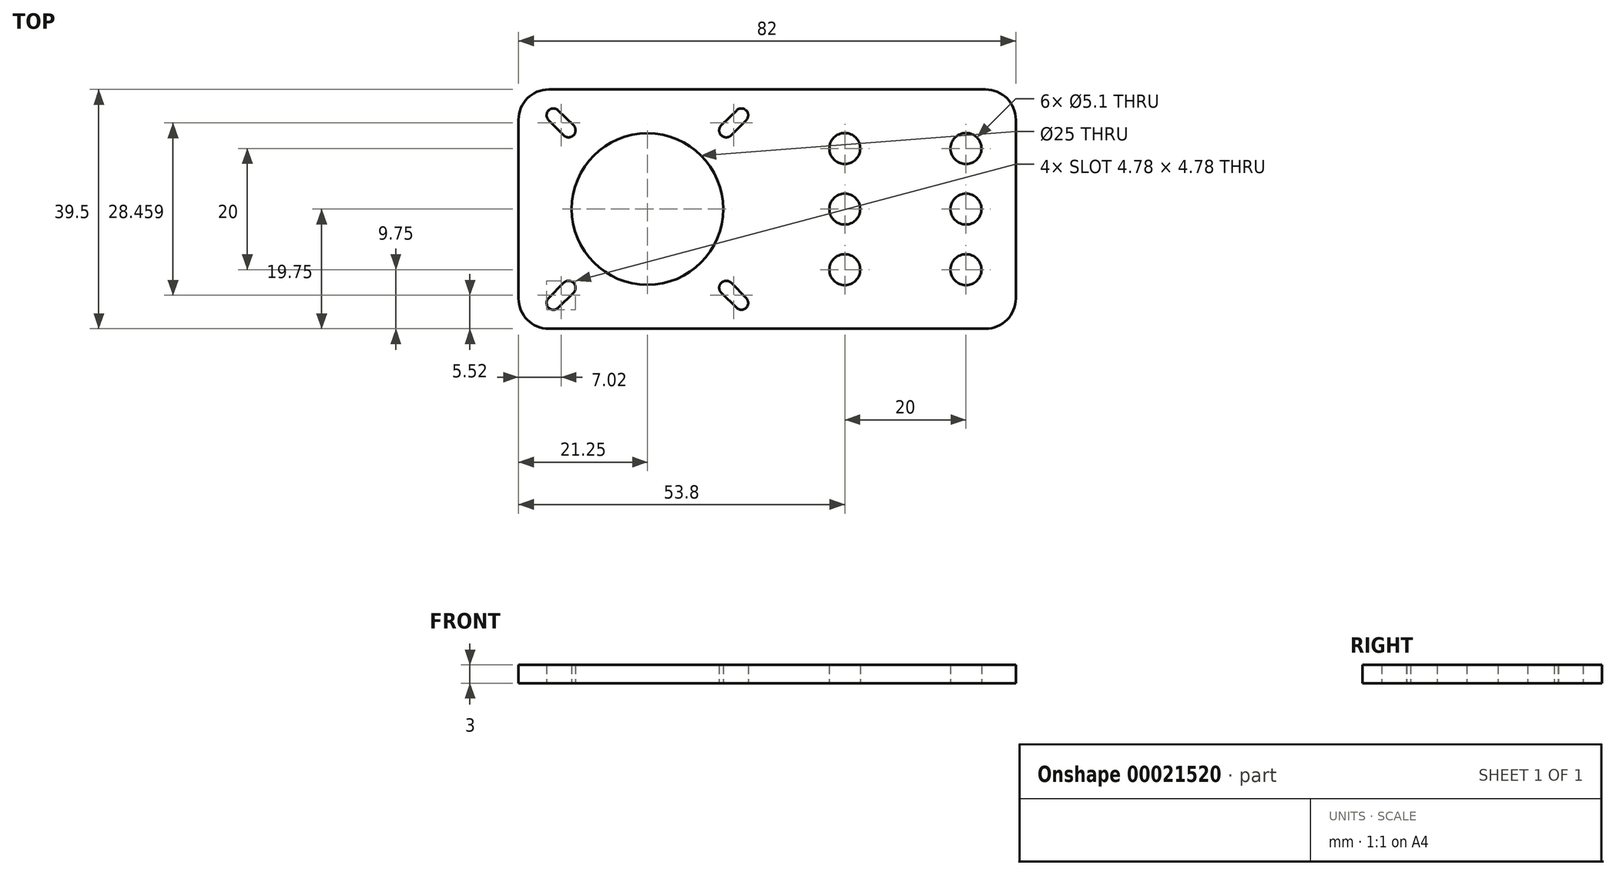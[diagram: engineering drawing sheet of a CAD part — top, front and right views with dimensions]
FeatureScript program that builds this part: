
annotation { "Feature Type Name" : "Feature", "Feature Type Description" : "" }
export const myFeature = defineFeature(function(context is Context, id is Id, definition is map)
    precondition{}
    {
        {
            var Q0;
            Q0=qCreatedBy(makeId("Top.planeOp"),FACE);
            var sketch = newSketch(context, id + "F0", { "sketchPlane" : qUnion([Q0])});
            skLineSegment(sketch, "E0.rect.bottom", {"start": v(36, -19.75) * mm, "end": v(-36, -19.75) * mm});
            skLineSegment(sketch, "E0.rect.top", {"start": v(36, 19.75) * mm, "end": v(-36, 19.75) * mm});
            skLineSegment(sketch, "E0.rect.left", {"start": v(41, -14.75) * mm, "end": v(41, 14.75) * mm});
            skLineSegment(sketch, "E0.rect.right", {"start": v(-41, -14.75) * mm, "end": v(-41, 14.75) * mm});
            skPoint(sketch, "E0.rect.middle", {"position": v(0, 0) * mm});
            skCircle(sketch, "E1", {"center": v(-19.75, 0) * mm, "radius": 12.5 * mm});
            skCircle(sketch, "E2", {"center": v(12.8, -10) * mm, "radius": 2.55 * mm});
            skCircle(sketch, "E3.0.1.0", {"center": v(12.8, 0) * mm, "radius": 2.55 * mm});
            skCircle(sketch, "E3.0.2.0", {"center": v(12.8, 10) * mm, "radius": 2.55 * mm});
            skCircle(sketch, "E3.1.0.0", {"center": v(32.8, -10) * mm, "radius": 2.55 * mm});
            skCircle(sketch, "E3.1.1.0", {"center": v(32.8, 0) * mm, "radius": 2.55 * mm});
            skCircle(sketch, "E3.1.2.0", {"center": v(32.8, 10) * mm, "radius": 2.55 * mm});
            skLineSegment(sketch, "E3.direction1", {"start": v(12.8, -10) * mm, "end": v(32.8, -10) * mm, "construction": true});
            skLineSegment(sketch, "E3.direction2", {"start": v(12.8, -10) * mm, "end": v(12.8, 0) * mm, "construction": true});
            skPoint(sketch, "E4.visualSharp", {"position": v(-41, 19.75) * mm});
            skArc(sketch, "E4.filletArc", {"start": v(-36, 19.75) * mm, "mid": v(-39.54, 18.29) * mm, "end": v(-41, 14.75) * mm});
            skPoint(sketch, "E5.visualSharp", {"position": v(41, 19.75) * mm});
            skArc(sketch, "E5.filletArc", {"start": v(41, 14.75) * mm, "mid": v(39.54, 18.29) * mm, "end": v(36, 19.75) * mm});
            skPoint(sketch, "E6.visualSharp", {"position": v(41, -19.75) * mm});
            skArc(sketch, "E6.filletArc", {"start": v(36, -19.75) * mm, "mid": v(39.54, -18.29) * mm, "end": v(41, -14.75) * mm});
            skPoint(sketch, "E7.visualSharp", {"position": v(-41, -19.75) * mm});
            skArc(sketch, "E7.filletArc", {"start": v(-41, -14.75) * mm, "mid": v(-39.54, -18.29) * mm, "end": v(-36, -19.75) * mm});
            skArc(sketch, "E8", {"start": v(-5.03, -16.3) * mm, "mid": v(-3.46, -16.3) * mm, "end": v(-3.45, -14.72) * mm});
            skArc(sketch, "E9", {"start": v(-5.92, -12.19) * mm, "mid": v(-7.57, -12.18) * mm, "end": v(-7.56, -13.83) * mm});
            skLineSegment(sketch, "E10", {"start": v(-5.92, -12.19) * mm, "end": v(-3.45, -14.72) * mm});
            skLineSegment(sketch, "E11", {"start": v(-7.56, -13.83) * mm, "end": v(-5.03, -16.3) * mm});
            skArc(sketch, "E12.1.0", {"start": v(-7.56, 13.83) * mm, "mid": v(-7.57, 12.18) * mm, "end": v(-5.92, 12.19) * mm});
            skLineSegment(sketch, "E12.1.1", {"start": v(-7.56, 13.83) * mm, "end": v(-5.03, 16.3) * mm});
            skArc(sketch, "E12.1.2", {"start": v(-3.45, 14.72) * mm, "mid": v(-3.46, 16.3) * mm, "end": v(-5.03, 16.3) * mm});
            skLineSegment(sketch, "E12.1.3", {"start": v(-5.92, 12.19) * mm, "end": v(-3.45, 14.72) * mm});
            skArc(sketch, "E12.2.0", {"start": v(-33.58, 12.19) * mm, "mid": v(-31.93, 12.18) * mm, "end": v(-31.94, 13.83) * mm});
            skLineSegment(sketch, "E12.2.1", {"start": v(-33.58, 12.19) * mm, "end": v(-36.05, 14.72) * mm});
            skArc(sketch, "E12.2.2", {"start": v(-34.47, 16.3) * mm, "mid": v(-36.04, 16.3) * mm, "end": v(-36.05, 14.72) * mm});
            skLineSegment(sketch, "E12.2.3", {"start": v(-31.94, 13.83) * mm, "end": v(-34.47, 16.3) * mm});
            skArc(sketch, "E12.3.0", {"start": v(-31.94, -13.83) * mm, "mid": v(-31.93, -12.18) * mm, "end": v(-33.58, -12.19) * mm});
            skLineSegment(sketch, "E12.3.1", {"start": v(-31.94, -13.83) * mm, "end": v(-34.47, -16.3) * mm});
            skArc(sketch, "E12.3.2", {"start": v(-36.05, -14.72) * mm, "mid": v(-36.04, -16.3) * mm, "end": v(-34.47, -16.3) * mm});
            skLineSegment(sketch, "E12.3.3", {"start": v(-33.58, -12.19) * mm, "end": v(-36.05, -14.72) * mm});
            skSolve(sketch);
        }
        {
            var Q0;
            Q0=makeQuery(id+"F0.imprint","IMPRINT",FACE,{"disambiguationData":[TD([[makeQuery(id+"F0.imprint","IMPRINT",EDGE,{"derivedFrom":sQuery(id+"F0.wireOp",EDGE,"E0.rect.bottom")}),-1.0]])]});
            extrude(context, id + "F1", {"entities" : qUnion([Q0]), "depth" : 3 * mm});
        }
    });
